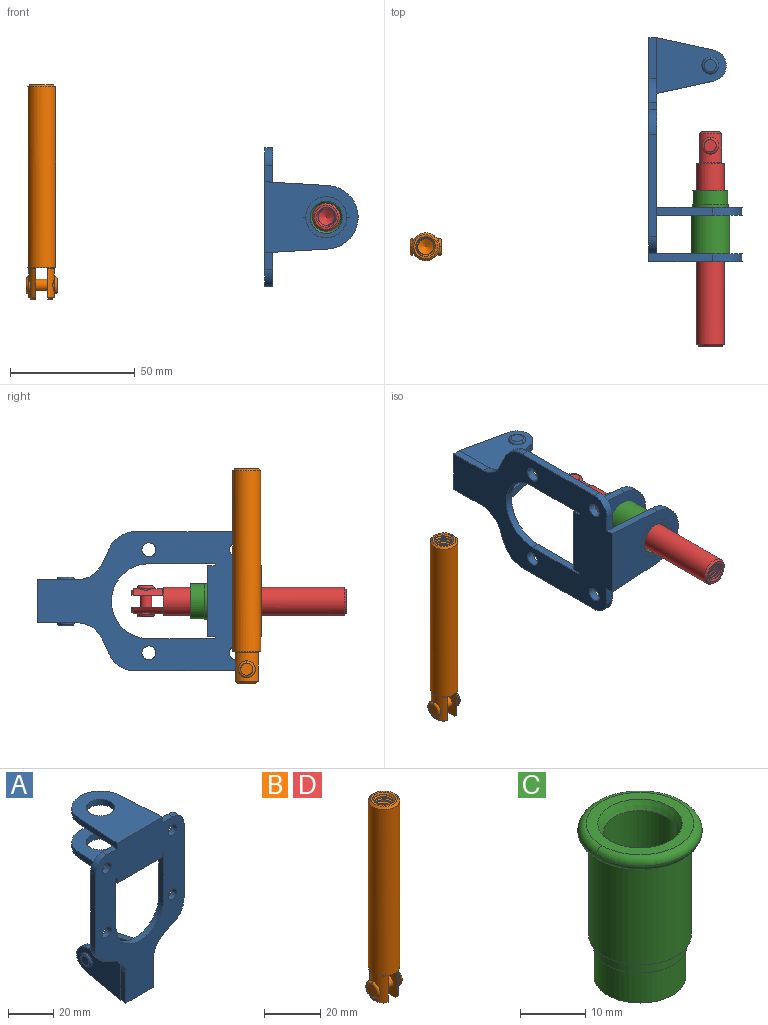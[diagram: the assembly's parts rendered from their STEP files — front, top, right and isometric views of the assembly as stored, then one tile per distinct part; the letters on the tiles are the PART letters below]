
ASSEMBLY  parts=4 mates=2
PART A: 55 faces, bbox 55.7x37.4x89.8 mm
  f0: torus R=2.41mm, axis (-1,0,0), area 15mm2, adj f11,f15,f25
  f1: torus R=2.41mm, axis (-1,0,0), area 15mm2, adj f10,f12,f22
  f2: cylinder r=2.78mm len=5.56mm, axis (0,-1,0), area 54.2mm2, adj f30,f54
  f3: cylinder r=14.99mm len=29.97mm, axis (0,-1,0), area 145.9mm2, adj f30,f49,f53,f54
  f4: cylinder r=2.78mm len=5.56mm, axis (0,-1,0), area 54.2mm2, adj f30,f54
  f5: cylinder r=2.78mm len=5.56mm, axis (0,-1,0), area 54.2mm2, adj f30,f54
  f6: cylinder r=2.78mm len=5.56mm, axis (0,-1,0), area 54.2mm2, adj f30,f54
  f7: cylinder r=6.35mm len=12.7mm, axis (0,0,1), area 123.6mm2, adj f27,f51
  f8: cylinder r=6.35mm len=12.7mm, axis (0,0,-1), area 124.7mm2, adj f21,f35
  f9: cylinder r=2.41mm len=11.18mm, axis (-1,0,0), area 169.4mm2, adj f16,f19
  f10: plane 4.83x4.83mm, normal (1,0,0), area 18.3mm2, adj f1,f12
  f11: plane 4.83x4.83mm, normal (-1,0,0), area 18.3mm2, adj f0,f15
  f12: torus R=2.41mm, axis (-1,0,0), area 15mm2, adj f1,f10,f22
  f13: cylinder r=6.35mm len=12.41mm, axis (1,0,0), area 53.4mm2, adj f18,f19,f22,f23
  f14: cylinder r=6.35mm len=12.41mm, axis (-1,0,0), area 53.4mm2, adj f16,f17,f24,f25
  f15: torus R=2.41mm, axis (-1,0,0), area 15mm2, adj f0,f11,f25
  f16: plane 27.86x22.35mm, normal (1,0,0), area 425.4mm2, adj f9,f14,f17,f24,f30
  f17: plane 22.86x4.97mm, normal (0,0.21,0.98), area 72.5mm2, adj f14,f16,f25,f30
  f18: plane 22.86x4.97mm, normal (0,0.21,0.98), area 72.5mm2, adj f13,f19,f22,f30
  f19: plane 27.86x22.35mm, normal (-1,0,0), area 425.4mm2, adj f9,f13,f18,f23,f30
  f20: cylinder r=12.7mm len=25.35mm, axis (0,0,-1), area 119.8mm2, adj f21,f34,f35,f36
  f21: plane 34.21x28.07mm, normal (0,0,-1), area 702.4mm2, adj f8,f20,f30,f34,f36
  f22: plane 27.96x22.45mm, normal (1,0,0), area 407.2mm2, adj f1,f12,f13,f18,f23,f30,f42,f43
  f23: plane 22.86x4.97mm, normal (0,0.21,-0.98), area 72.5mm2, adj f13,f19,f22,f44
  f24: plane 22.86x4.97mm, normal (0,0.21,-0.98), area 72.5mm2, adj f14,f16,f25,f44
  f25: plane 27.86x22.35mm, normal (-1,0,0), area 407.1mm2, adj f0,f14,f15,f17,f24,f30,f45,f46
  f26: plane 3.1x0.95mm, normal (0,0,-1), area 2.7mm2, adj f30,f49,f50,f54
  f27: plane 34.21x28.07mm, normal (0,0,1), area 702.4mm2, adj f7,f28,f30,f50,f52
  f28: cylinder r=12.7mm len=25.35mm, axis (0,0,1), area 118.8mm2, adj f27,f50,f51,f52
  f29: plane 3.1x0.95mm, normal (0,0,-1), area 2.7mm2, adj f30,f52,f53,f54
  f30: plane 86.54x55.63mm, normal (0,1,0), area 2362.9mm2, adj f2,f3,f4,f5,f6,f16,f17,f18
  f31: plane 40.56x3.1mm, normal (-1,0,0), area 125.7mm2, adj f30,f32,f48,f54
  f32: cylinder r=7.11mm len=7.11mm, axis (0,-1,0), area 34.6mm2, adj f30,f31,f33,f54
  f33: plane 6.67x3.1mm, normal (0,0,1), area 20.4mm2, adj f30,f32,f34,f54
  f34: plane 25.39x3.13mm, normal (-1,0.06,0), area 79.5mm2, adj f20,f21,f33,f35,f54
  f35: plane 37.31x28.45mm, normal (0,0,1), area 789.9mm2, adj f8,f20,f34,f36,f54
  f36: plane 25.39x3.13mm, normal (1,0.06,0), area 79.5mm2, adj f20,f21,f35,f37,f54
  f37: plane 6.67x3.1mm, normal (0,0,1), area 20.4mm2, adj f30,f36,f38,f54
  f38: cylinder r=7.11mm len=7.11mm, axis (0,-1,0), area 34.6mm2, adj f30,f37,f39,f54
  f39: plane 40.56x3.1mm, normal (1,0,0), area 125.7mm2, adj f30,f38,f40,f54
  f40: cylinder r=11.18mm len=10.16mm, axis (0,-1,0), area 39.5mm2, adj f30,f39,f41,f54
  f41: plane 6.09x3.1mm, normal (0.42,0,-0.91), area 20.8mm2, adj f30,f40,f42,f54
  f42: cylinder r=11.18mm len=9.41mm, axis (0,-1,0), area 37.2mm2, adj f22,f30,f41,f43,f54
  f43: plane 16.5x3.1mm, normal (1,0,0), area 51.1mm2, adj f22,f42,f44,f54
  f44: plane 17.37x3.1mm, normal (0,0,-1), area 53.8mm2, adj f23,f24,f30,f43,f45,f54
  f45: plane 16.5x3.1mm, normal (-1,0,0), area 51.1mm2, adj f25,f44,f46,f54
  f46: cylinder r=11.18mm len=9.41mm, axis (0,-1,0), area 37.2mm2, adj f25,f30,f45,f47,f54
  f47: plane 6.09x3.1mm, normal (-0.42,0,-0.91), area 20.8mm2, adj f30,f46,f48,f54
  f48: cylinder r=11.18mm len=10.16mm, axis (0,-1,0), area 39.5mm2, adj f30,f31,f47,f54
  f49: plane 26.54x3.1mm, normal (-1,0,0), area 82.3mm2, adj f3,f26,f30,f54
  f50: plane 25.39x3.1mm, normal (1,0.06,0), area 78.8mm2, adj f26,f27,f28,f51,f54
  f51: plane 37.31x28.45mm, normal (0,0,-1), area 789.9mm2, adj f7,f28,f50,f52,f54
  f52: plane 25.39x3.1mm, normal (-1,0.06,0), area 78.8mm2, adj f27,f28,f29,f51,f54
  f53: plane 26.54x3.1mm, normal (1,0,0), area 82.3mm2, adj f3,f29,f30,f54
  f54: plane 89.66x55.63mm, normal (0,-1,0), area 2678.5mm2, adj f2,f3,f4,f5,f6,f26,f29,f31
PART B: 48 faces, bbox 12.6x11.1x86.1 mm
  f0: torus R=2.41mm, axis (-1,0,0), area 15mm2, adj f30,f32,f34
  f1: torus R=2.41mm, axis (-1,0,0), area 15mm2, adj f29,f31,f33
  f2: cylinder r=5.54mm len=72.39mm, axis (0,0,1), area 2518.5mm2, adj f3,f4,f42,f43
  f3: cone r=5.54mm half-angle=45deg, axis (0,0,1), area 7.6mm2, adj f2,f5,f41
  f4: cone r=5.54mm half-angle=45deg, axis (0,0,-1), area 34.9mm2, adj f2,f39
  f5: cylinder r=5.08mm len=11.48mm, axis (0,0,1), area 108.3mm2, adj f3,f7,f8,f41
  f6: cylinder r=2.41mm len=4.83mm, axis (-1,0,0), area 71.2mm2, adj f40,f41
  f7: cylinder r=2.41mm len=4.83mm, axis (-1,0,0), area 7.6mm2, adj f5,f34
  f8: cone r=5.08mm half-angle=45deg, axis (0,0,1), area 10.6mm2, adj f5,f37,f41
  f9: cone r=3.98mm half-angle=45deg, axis (0,0,1), area 17.6mm2, adj f27,f39,f45,f46,f47
  f10: cylinder r=2.41mm len=4.83mm, axis (-1,0,0), area 7.6mm2, adj f33,f38
  f11: cylinder r=3.2mm len=6.4mm, axis (0,0,1), area 78.4mm2, adj f12,f28,f44,f45,f47
  f12: cylinder r=3.2mm len=6.4mm, axis (0,0,1), area 10.5mm2, adj f11,f13,f45,f47
  f13: cylinder r=3.2mm len=6.4mm, axis (0,0,1), area 10.5mm2, adj f12,f14,f45,f47
  f14: cylinder r=3.2mm len=6.4mm, axis (0,0,1), area 10.5mm2, adj f13,f15,f45,f47
  f15: cylinder r=3.2mm len=6.4mm, axis (0,0,1), area 10.5mm2, adj f14,f16,f45,f47
  f16: cylinder r=3.2mm len=6.4mm, axis (0,0,1), area 10.5mm2, adj f15,f17,f45,f47
  f17: cylinder r=3.2mm len=6.4mm, axis (0,0,1), area 10.5mm2, adj f16,f18,f45,f47
  f18: cylinder r=3.2mm len=6.4mm, axis (0,0,1), area 10.5mm2, adj f17,f19,f45,f47
  f19: cylinder r=3.2mm len=6.4mm, axis (0,0,1), area 10.5mm2, adj f18,f20,f45,f47
  f20: cylinder r=3.2mm len=6.4mm, axis (0,0,1), area 10.5mm2, adj f19,f21,f45,f47
  f21: cylinder r=3.2mm len=6.4mm, axis (0,0,1), area 10.5mm2, adj f20,f22,f45,f47
  f22: cylinder r=3.2mm len=6.4mm, axis (0,0,1), area 10.5mm2, adj f21,f23,f45,f47
  f23: cylinder r=3.2mm len=6.4mm, axis (0,0,1), area 10.5mm2, adj f22,f24,f45,f47
  f24: cylinder r=3.2mm len=6.4mm, axis (0,0,1), area 10.5mm2, adj f23,f25,f45,f47
  f25: cylinder r=3.2mm len=6.4mm, axis (0,0,1), area 10.5mm2, adj f24,f26,f45,f47
  f26: cylinder r=3.2mm len=6.4mm, axis (0,0,1), area 10.5mm2, adj f25,f27,f45,f47
  f27: cylinder r=3.2mm len=6.4mm, axis (0,0,1), area 7.4mm2, adj f9,f26,f45,f47
  f28: cone r=3.2mm half-angle=60deg, axis (0,0,1), area 37.2mm2, adj f11
  f29: plane 4.83x4.83mm, normal (-1,0,0), area 18.3mm2, adj f1,f31
  f30: plane 4.83x4.83mm, normal (1,0,0), area 18.3mm2, adj f0,f32
  f31: torus R=2.41mm, axis (-1,0,0), area 15mm2, adj f1,f29,f33
  f32: torus R=2.41mm, axis (-1,0,0), area 15mm2, adj f0,f30,f34
  f33: plane 6.83x6.83mm, normal (1,0,0), area 18.3mm2, adj f1,f10,f31
  f34: plane 6.83x6.83mm, normal (-1,0,0), area 18.3mm2, adj f0,f7,f32
  f35: cone r=5.08mm half-angle=45deg, axis (0,0,1), area 10.6mm2, adj f36,f38,f40
  f36: plane 7.25x1.97mm, normal (0,0,-1), area 10mm2, adj f35,f40
  f37: plane 7.25x1.97mm, normal (0,0,-1), area 10mm2, adj f8,f41
  f38: cylinder r=5.08mm len=11.48mm, axis (0,0,1), area 108.3mm2, adj f10,f35,f40,f42
  f39: plane 9.55x9.55mm, normal (0,0,1), area 22mm2, adj f4,f9
  f40: plane 12.76x10.09mm, normal (1,0,0), area 95.7mm2, adj f6,f35,f36,f38,f42,f43
  f41: plane 12.76x10.09mm, normal (-1,0,0), area 95.7mm2, adj f3,f5,f6,f8,f37,f43
  f42: cone r=5.54mm half-angle=45deg, axis (0,0,1), area 7.6mm2, adj f2,f38,f40
  f43: plane 11.07x4.7mm, normal (0,0,-1), area 50.4mm2, adj f2,f40,f41
  f44: plane 0.89x0.62mm, normal (-1,0,0), area 0.3mm2, adj f11,f45,f46,f47
  f45: bspline ~24.8x7.63mm, area 266.6mm2, adj f9,f11,f12,f13,f14,f15,f16,f17
  f46: bspline ~24.87x7.63mm, area 73.6mm2, adj f9,f44,f45,f47
  f47: bspline ~24.98x7.63mm, area 272.5mm2, adj f9,f11,f12,f13,f14,f15,f16,f17
PART C: 15 faces, bbox 20.6x20.6x28.7 mm
  f0: torus R=8.26mm, axis (0,0,1), area 56.8mm2, adj f1,f10,f12
  f1: torus R=8.26mm, axis (0,0,1), area 56.8mm2, adj f0,f6,f13
  f2: cylinder r=5.59mm len=25.91mm, axis (0,0,1), area 909.6mm2, adj f3,f4
  f3: cone r=6.86mm half-angle=45deg, axis (0,0,-1), area 70.2mm2, adj f2,f14
  f4: cone r=6.47mm half-angle=30deg, axis (0,0,1), area 66.7mm2, adj f2,f13
  f5: cylinder r=7.04mm len=14.07mm, axis (0,0,1), area 252.6mm2, adj f11,f14
  f6: torus R=8.26mm, axis (0,0,1), area 56.8mm2, adj f1,f12,f13
  f7: cylinder r=7.16mm len=14.33mm, axis (0,0,1), area 91.5mm2, adj f9,f11
  f8: cylinder r=7.86mm len=18.42mm, axis (0,0,1), area 909.6mm2, adj f9,f10
  f9: plane 15.72x15.72mm, normal (0,0,-1), area 33mm2, adj f7,f8
  f10: plane 16.51x16.51mm, normal (0,0,-1), area 19.9mm2, adj f0,f8,f12
  f11: plane 14.33x14.33mm, normal (0,0,-1), area 5.7mm2, adj f5,f7
  f12: torus R=8.26mm, axis (0,0,1), area 56.8mm2, adj f0,f6,f10
  f13: plane 16.51x16.51mm, normal (0,0,1), area 82.7mm2, adj f1,f4,f6
  f14: plane 14.07x14.07mm, normal (0,0,-1), area 7.8mm2, adj f3,f5
PART D: same geometry as B
PLACE A rot(axis=(0.58,0.58,-0.58),120deg) t=(-3.06,-7.81,19.76)mm fixed
PLACE B t=(-92.32,-72.82,-22.94)mm
PLACE C rot(axis=(1,0,0),90deg) t=(21.55,-5.27,-4.85)mm
PLACE D rot(axis=(0.58,0.58,-0.58),120deg) t=(-3.06,7.7,19.76)mm
MATE fastened D.f2 <-> A.f7  axis (0,-1,0) through (21.55,-51.08,19.76)mm
MATE fastened A.f7 <-> C.f2  axis (0,-1,0) through (21.55,-54.2,19.76)mm
